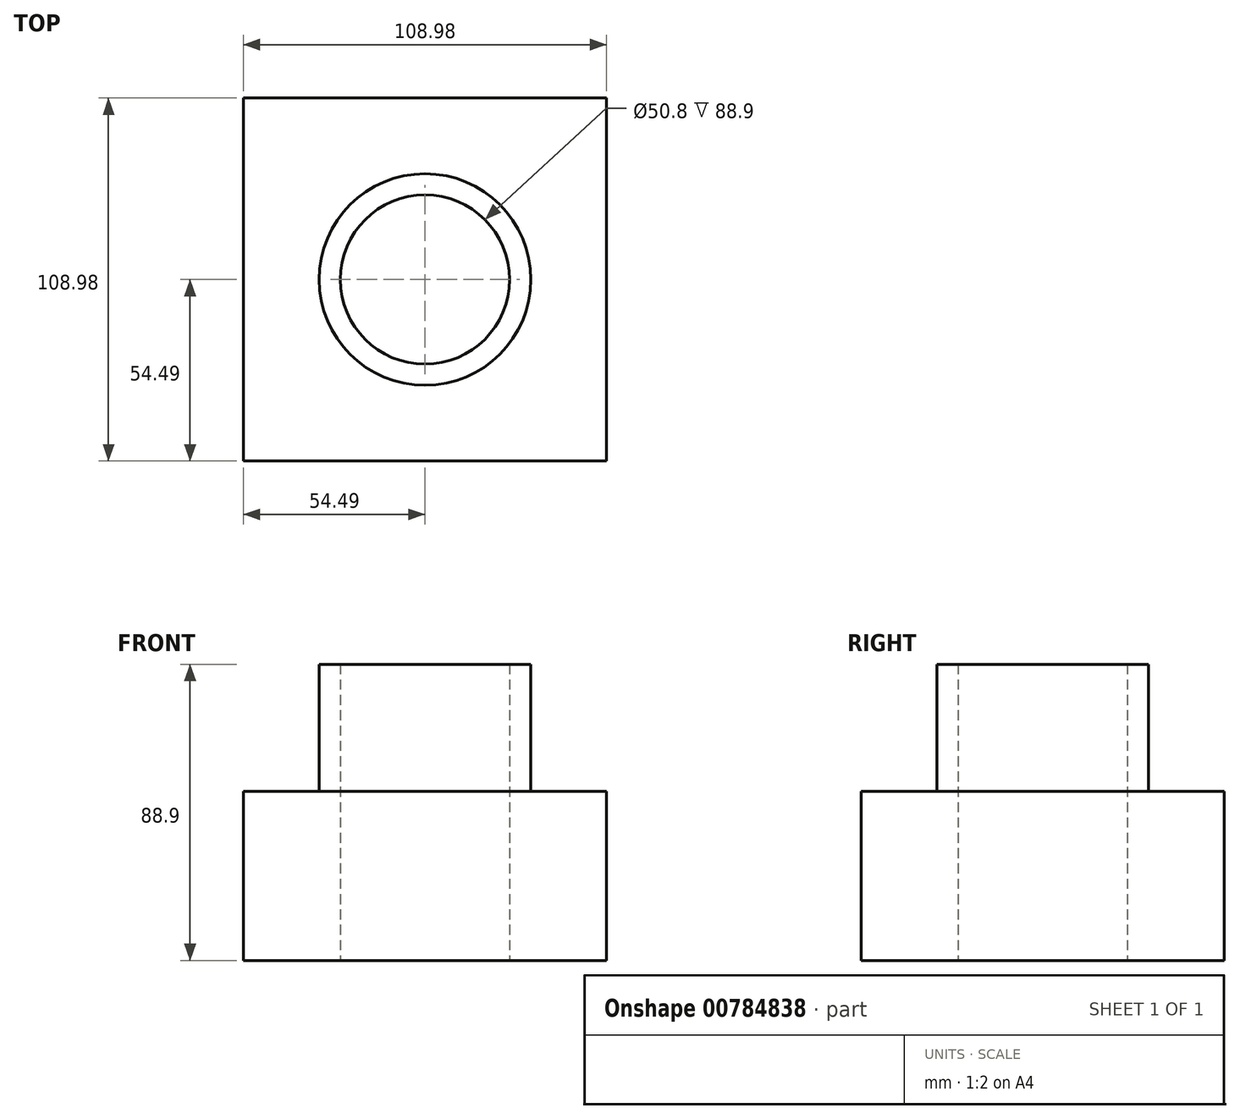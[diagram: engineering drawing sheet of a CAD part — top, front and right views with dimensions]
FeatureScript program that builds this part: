
annotation { "Feature Type Name" : "Feature", "Feature Type Description" : "" }
export const myFeature = defineFeature(function(context is Context, id is Id, definition is map)
    precondition{}
    {
        {
            var Q0;
            Q0=qCreatedBy(makeId("Top.planeOp"),FACE);
            var sketch = newSketch(context, id + "F0", { "sketchPlane" : qUnion([Q0])});
            skLineSegment(sketch, "E0.bottom", {"start": v(-54.49, 54.49) * mm, "end": v(54.49, 54.49) * mm});
            skLineSegment(sketch, "E0.top", {"start": v(-54.49, -54.49) * mm, "end": v(54.49, -54.49) * mm});
            skLineSegment(sketch, "E0.left", {"start": v(-54.49, 54.49) * mm, "end": v(-54.49, -54.49) * mm});
            skLineSegment(sketch, "E0.right", {"start": v(54.49, 54.49) * mm, "end": v(54.49, -54.49) * mm});
            skCircle(sketch, "E1", {"center": v(0, 0) * mm, "radius": 31.75 * mm});
            skCircle(sketch, "E2", {"center": v(0, 0) * mm, "radius": 25.4 * mm});
            skSolve(sketch);
        }
        {
            var Q0;
            Q0=makeQuery(id+"F0.imprint","IMPRINT",FACE,{"disambiguationData":[TD([[makeQuery(id+"F0.imprint","IMPRINT",EDGE,{"derivedFrom":sQuery(id+"F0.wireOp",EDGE,"E0.bottom")}),-1.0]])]});
            extrude(context, id + "F1", {"entities" : qUnion([Q0]), "depth" : 50.8 * mm, "offsetDistance" : 25.4 * mm});
        }
        {
            var Q0;
            Q0=makeQuery(id+"F0.imprint","IMPRINT",FACE,{"disambiguationData":[TD([[makeQuery(id+"F0.imprint","IMPRINT",EDGE,{"derivedFrom":sQuery(id+"F0.wireOp",EDGE,"E1")}),1.0]])]});
            extrude(context, id + "F2", {"entities" : qUnion([Q0]), "operationType" : NewBodyOperationType.ADD, "depth" : 88.9 * mm, "offsetDistance" : 25.4 * mm});
        }
    });
